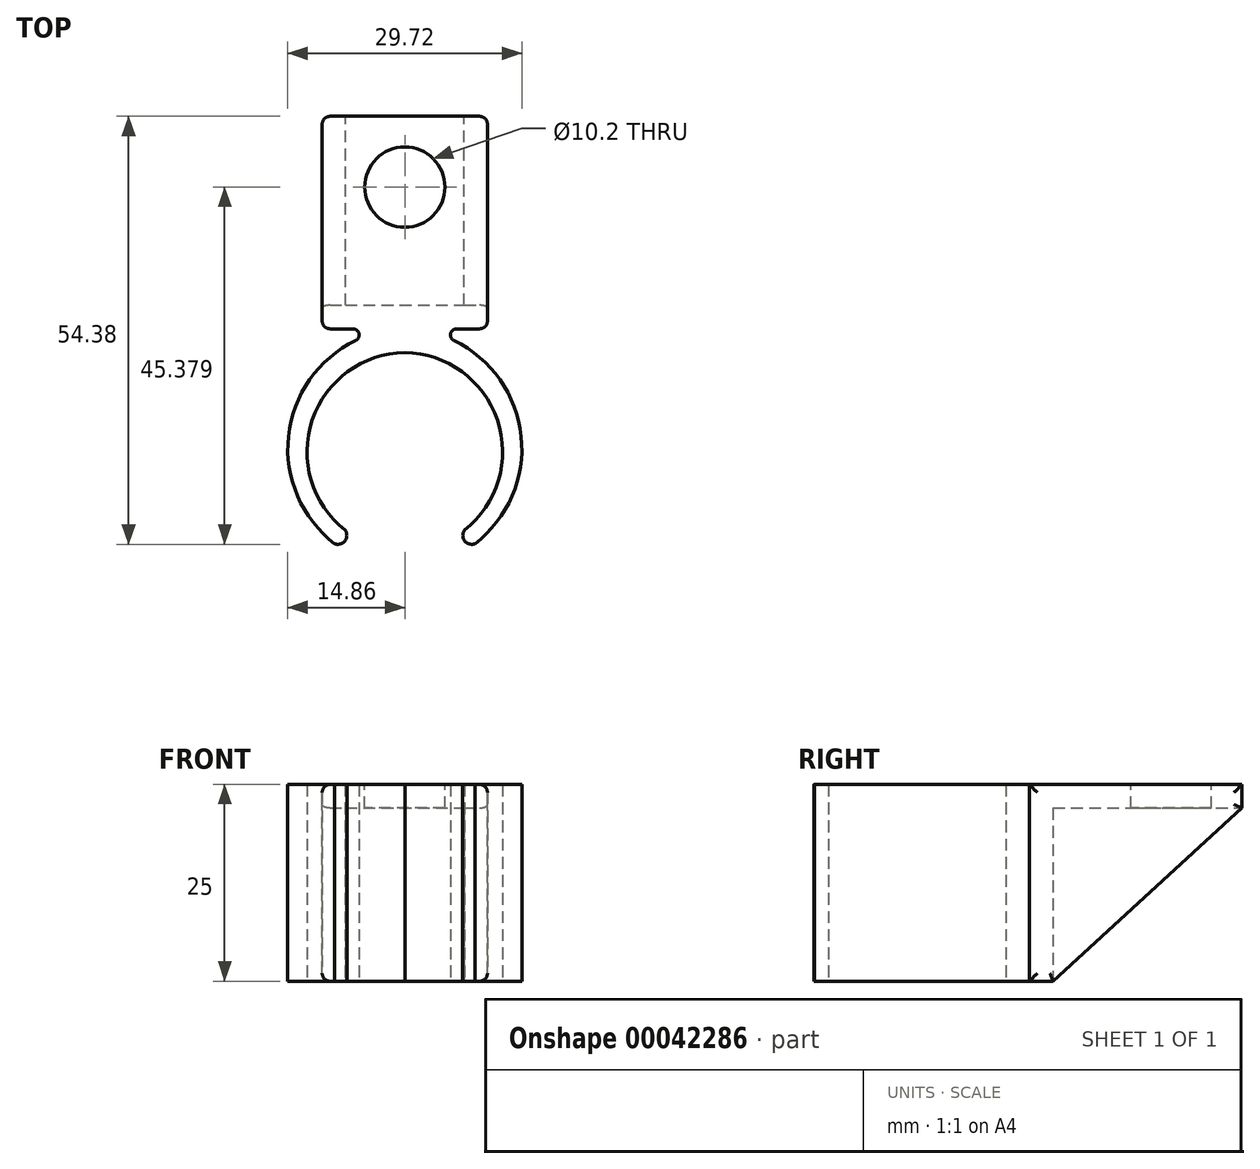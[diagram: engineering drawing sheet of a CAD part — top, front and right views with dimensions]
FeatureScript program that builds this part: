
annotation { "Feature Type Name" : "Feature", "Feature Type Description" : "" }
export const myFeature = defineFeature(function(context is Context, id is Id, definition is map)
    precondition{}
    {
        {
            var Q0;
            Q0=qCreatedBy(makeId("Top.planeOp"),FACE);
            var sketch = newSketch(context, id + "F0", { "sketchPlane" : qUnion([Q0])});
            skCircle(sketch, "E0", {"center": v(0, 0) * mm, "radius": 13.5 * mm, "construction": true});
            skCircle(sketch, "E1", {"center": v(0, 0) * mm, "radius": 11 * mm, "construction": true});
            skLineSegment(sketch, "E2", {"start": v(0, 0) * mm, "end": v(8.68, -10.34) * mm, "construction": true});
            skArc(sketch, "E3.0", {"start": v(8.9, -10.8) * mm, "mid": v(14.78, 2.84) * mm, "end": v(6.24, 15) * mm});
            skLineSegment(sketch, "E4", {"start": v(6.58, 16.5) * mm, "end": v(10.5, 16.5) * mm});
            skLineSegment(sketch, "E5", {"start": v(-10.5, 16.5) * mm, "end": v(-10.5, 19.5) * mm});
            skLineSegment(sketch, "E6", {"start": v(-10.5, 19.5) * mm, "end": v(10.5, 19.5) * mm});
            skLineSegment(sketch, "E7", {"start": v(10.5, 19.5) * mm, "end": v(10.5, 16.5) * mm});
            skArc(sketch, "E8.filletArc", {"start": v(6.58, 16.5) * mm, "mid": v(5.81, 15.89) * mm, "end": v(6.24, 15) * mm});
            skArc(sketch, "E9.MirrorCS", {"start": v(-6.58, 16.5) * mm, "mid": v(-5.81, 15.89) * mm, "end": v(-6.24, 15) * mm});
            skLineSegment(sketch, "E10.trimOffspring", {"start": v(-6.58, 16.5) * mm, "end": v(-10.5, 16.5) * mm});
            skArc(sketch, "E11", {"start": v(7.6, -9.05) * mm, "mid": v(11.76, 4.9) * mm, "end": v(0, 13.5) * mm});
            skPoint(sketch, "E12.orphan", {"position": v(7.07, -8.43) * mm});
            skPoint(sketch, "E13.orphan", {"position": v(-7.07, -8.43) * mm});
            skPoint(sketch, "E14.MirrorCS.start.orphan", {"position": v(-8.9, -10.8) * mm});
            skPoint(sketch, "E15.MirrorCS.end.orphan", {"position": v(0, 13.5) * mm});
            skArc(sketch, "E16", {"start": v(7.6, -9.05) * mm, "mid": v(7.59, -10.41) * mm, "end": v(8.9, -10.8) * mm});
            skArc(sketch, "E17.MirrorCS", {"start": v(-7.6, -9.05) * mm, "mid": v(-11.76, 4.9) * mm, "end": v(0, 13.5) * mm});
            skArc(sketch, "E18.MirrorCS", {"start": v(-8.9, -10.8) * mm, "mid": v(-14.78, 2.84) * mm, "end": v(-6.24, 15) * mm});
            skArc(sketch, "E19.MirrorCS", {"start": v(-7.6, -9.05) * mm, "mid": v(-7.59, -10.41) * mm, "end": v(-8.9, -10.8) * mm});
            skSolve(sketch);
        }
        {
            var Q0;
            Q0=qSketchRegion(id+"F0",true);
            extrude(context, id + "F1", {"entities" : qUnion([Q0]), "depth" : 25 * mm});
        }
        {
            var Q0;
            Q0=makeQuery(id+"F1.opExtrude","CAP_FACE",FACE,{"disambiguationData":[OSD([sQuery(id+"F0.wireOp",EDGE,"fddaa1e2-854d-42ac-9923-583dc186ed8e"),sQuery(id+"F0.wireOp",EDGE,"E3.0"),sQuery(id+"F0.wireOp",EDGE,"6ffdca8f-1516-4eb4-be9d-7194918c999f"),sQuery(id+"F0.wireOp",EDGE,"E14.MirrorCS"),sQuery(id+"F0.wireOp",EDGE,"E15.MirrorCS"),sQuery(id+"F0.wireOp",EDGE,"ee1b03d7-64c2-4d08-9048-61b7a477a1140.MirrorCS"),sQuery(id+"F0.wireOp",EDGE,"E4"),sQuery(id+"F0.wireOp",EDGE,"E5"),sQuery(id+"F0.wireOp",EDGE,"E6"),sQuery(id+"F0.wireOp",EDGE,"E7"),sQuery(id+"F0.wireOp",EDGE,"E8.filletArc"),sQuery(id+"F0.wireOp",EDGE,"E9.MirrorCS"),sQuery(id+"F0.wireOp",EDGE,"E10.trimOffspring")])],"isStart":false});
            var sketch = newSketch(context, id + "F2", { "sketchPlane" : qUnion([Q0])});
            skLineSegment(sketch, "E20.bottom", {"start": v(-10.5, 19.5) * mm, "end": v(10.5, 19.5) * mm});
            skLineSegment(sketch, "E20.top", {"start": v(-10.5, 43.5) * mm, "end": v(10.5, 43.5) * mm});
            skLineSegment(sketch, "E20.left", {"start": v(-10.5, 19.5) * mm, "end": v(-10.5, 43.5) * mm});
            skLineSegment(sketch, "E20.right", {"start": v(10.5, 19.5) * mm, "end": v(10.5, 43.5) * mm});
            skCircle(sketch, "E21", {"center": v(0, 34.5) * mm, "radius": 5.1 * mm});
            skSolve(sketch);
        }
        {
            var Q0;
            Q0=qSketchRegion(id+"F2",true);
            extrude(context, id + "F3", {"entities" : qUnion([Q0]), "oppositeDirection" : true, "depth" : 3 * mm});
        }
        {
            var Q0;
            Q0=makeQuery(id+"F3.opExtrude","SWEPT_BODY",BODY,{"disambiguationData":[OSD([sQuery(id+"F2.wireOp",EDGE,"E20.bottom"),sQuery(id+"F2.wireOp",EDGE,"E20.top"),sQuery(id+"F2.wireOp",EDGE,"E20.left"),sQuery(id+"F2.wireOp",EDGE,"E20.right")])]});
            var Q1;
            Q1=makeQuery(id+"F1.opExtrude","SWEPT_BODY",BODY,{"disambiguationData":[OSD([sQuery(id+"F0.wireOp",EDGE,"fddaa1e2-854d-42ac-9923-583dc186ed8e"),sQuery(id+"F0.wireOp",EDGE,"E3.0"),sQuery(id+"F0.wireOp",EDGE,"6ffdca8f-1516-4eb4-be9d-7194918c999f"),sQuery(id+"F0.wireOp",EDGE,"E14.MirrorCS"),sQuery(id+"F0.wireOp",EDGE,"E15.MirrorCS"),sQuery(id+"F0.wireOp",EDGE,"ee1b03d7-64c2-4d08-9048-61b7a477a1140.MirrorCS"),sQuery(id+"F0.wireOp",EDGE,"E4"),sQuery(id+"F0.wireOp",EDGE,"E5"),sQuery(id+"F0.wireOp",EDGE,"E6"),sQuery(id+"F0.wireOp",EDGE,"E7"),sQuery(id+"F0.wireOp",EDGE,"E8.filletArc"),sQuery(id+"F0.wireOp",EDGE,"E9.MirrorCS"),sQuery(id+"F0.wireOp",EDGE,"E10.trimOffspring")])]});
            booleanBodies(context, id + "F4", {"operationType" : BooleanOperationType.UNION, "tools" : qUnion([Q0, Q1])});
        }
        {
            var Q0;
            Q0=makeQuery(id+"F4.opBoolean","MERGE",FACE,{"derivedFrom":[makeQuery(id+"F1.opExtrude","SWEPT_FACE",FACE,{"disambiguationData":[OSD([sQuery(id+"F0.wireOp",EDGE,"E7")])]}),makeQuery(id+"F3.opExtrude","SWEPT_FACE",FACE,{"disambiguationData":[OSD([sQuery(id+"F2.wireOp",EDGE,"E20.right")])]})]});
            var sketch = newSketch(context, id + "F5", { "sketchPlane" : qUnion([Q0])});
            skLineSegment(sketch, "E22", {"start": v(19.5, 0) * mm, "end": v(43.5, 22) * mm});
            skLineSegment(sketch, "E23", {"start": v(43.5, 22) * mm, "end": v(19.5, 22) * mm});
            skLineSegment(sketch, "E24", {"start": v(19.5, 22) * mm, "end": v(19.5, 0) * mm});
            skSolve(sketch);
        }
        {
            var Q0;
            Q0=qSketchRegion(id+"F5",true);
            extrude(context, id + "F6", {"entities" : qUnion([Q0]), "oppositeDirection" : true, "depth" : 2.95 * mm});
        }
        {
            var Q0;
            Q0=makeQuery(id+"F6.opExtrude","SWEPT_BODY",BODY,{"disambiguationData":[OSD([sQuery(id+"F5.wireOp",EDGE,"E22"),sQuery(id+"F5.wireOp",EDGE,"E23"),sQuery(id+"F5.wireOp",EDGE,"E24")])]});
            var Q1;
            Q1=qCreatedBy(makeId("Right.planeOp"),FACE);
            mirror(context, id + "F7", {"operationType" : NewBodyOperationType.ADD, "entities" : qUnion([Q0]), "mirrorPlane" : qUnion([Q1])});
        }
        {
            var Q0;
            Q0=makeQuery(id+"F7.boolean.opBoolean","MERGE",FACE,{"derivedFrom":[makeQuery(id+"F4.opBoolean","MERGE",FACE,{"derivedFrom":[makeQuery(id+"F1.opExtrude","SWEPT_FACE",FACE,{"disambiguationData":[OSD([sQuery(id+"F0.wireOp",EDGE,"E7")])]}),makeQuery(id+"F3.opExtrude","SWEPT_FACE",FACE,{"disambiguationData":[OSD([sQuery(id+"F2.wireOp",EDGE,"E20.right")])]})]}),makeQuery(id+"F6.opExtrude","CAP_FACE",FACE,{"disambiguationData":[OSD([sQuery(id+"F5.wireOp",EDGE,"E22"),sQuery(id+"F5.wireOp",EDGE,"E23"),sQuery(id+"F5.wireOp",EDGE,"E24")])],"isStart":true})]});
            var Q1;
            Q1=makeQuery(id+"F7.boolean.opBoolean","MERGE",FACE,{"derivedFrom":[makeQuery(id+"F4.opBoolean","MERGE",FACE,{"derivedFrom":[makeQuery(id+"F1.opExtrude","SWEPT_FACE",FACE,{"disambiguationData":[OSD([sQuery(id+"F0.wireOp",EDGE,"E5")])]}),makeQuery(id+"F3.opExtrude","SWEPT_FACE",FACE,{"disambiguationData":[OSD([sQuery(id+"F2.wireOp",EDGE,"E20.left")])]})]}),makeQuery(id+"F7.opPattern","COPY",FACE,{"derivedFrom":makeQuery(id+"F6.opExtrude","CAP_FACE",FACE,{"disambiguationData":[OSD([sQuery(id+"F5.wireOp",EDGE,"E22"),sQuery(id+"F5.wireOp",EDGE,"E23"),sQuery(id+"F5.wireOp",EDGE,"E24")])],"isStart":true}),"instanceName":"1"})]});
            fillet(context, id + "F8", {"entities" : qUnion([Q0, Q1]), "radius" : 1 * mm, "tangentPropagation" : true, "allowEdgeOverflow" : false});
        }
    });
